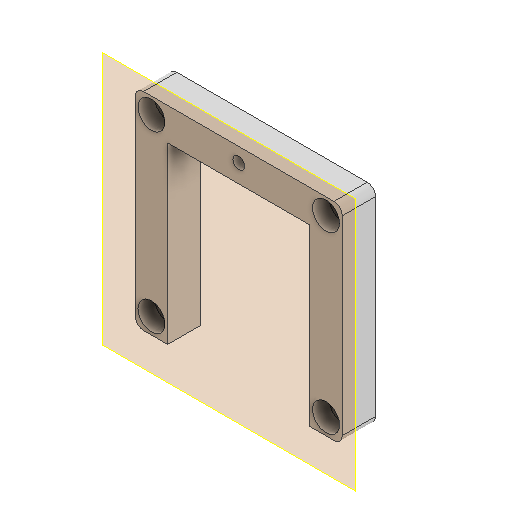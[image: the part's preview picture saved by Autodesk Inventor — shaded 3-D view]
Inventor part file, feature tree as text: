
AUTODESK INVENTOR PART (.ipt)
format: ipt  version: 2023 (Build 270158000, 158)  size: 185,856 bytes
history: native  units: mm
features: sketch x4, reference x4, other x4, extrude x2, hole x2, plane x1, projected_geometry x1
ambient origin geometry x8: Origin, YZ Plane, XZ Plane, XY Plane, X Axis, Y Axis, Z Axis, Center Point
bodies: Solid1 (feature_tree)
feature tree (18):
  extrude  "Extrusion1"  Depth=8.0mm TaperAngle=0.0deg
  extrude  "Extrusion2"  Depth=3.4mm
  plane  "Arbeitsebene1"
  hole  "Bohrung1"  [1 undecoded]
  hole  "Bohrung2"  [1 undecoded]
  sketch  "Sketch1"  dims[d0=7.8mm d1=8.0mm d2=0.0mm]
  reference  "Reference1"
  reference  "Reference2"
  reference  "Reference3"
  sketch  "Sketch2"  dims[d3=2.8mm d4=3.4mm]
  sketch  "Skizze3"  dims[d5=8.0mm d6=0.0mm]
  reference  "Referenz4"
  sketch  "Skizze4"  dims[d7=4.6mm d8=6.0mm d9=4.0mm d10=2.0mm d11=90.0deg d12=8.0mm d13=20.594885mm d14=3.0mm d15=6.0mm d16=6.5mm d17=4.0mm d18=90.0deg d19=8.0mm d20=20.594885mm]
  projected_geometry  "Projizierte Kontur1"
  other  "Assembly_Cube_Z-Stage_NEMA11_china_Borstel.iam"
  other  "00_Linear_Stage_NEMA11_Mount:1"
  other  "10_Base_puzzle_v3:2"
  other  "10_Base_puzzle_IM:2"
note: 2 required parameter values undecoded (feature->parameter linkage not recoverable at this tier; creation-order binding heuristic only, values carry confidence <= 0.55)
